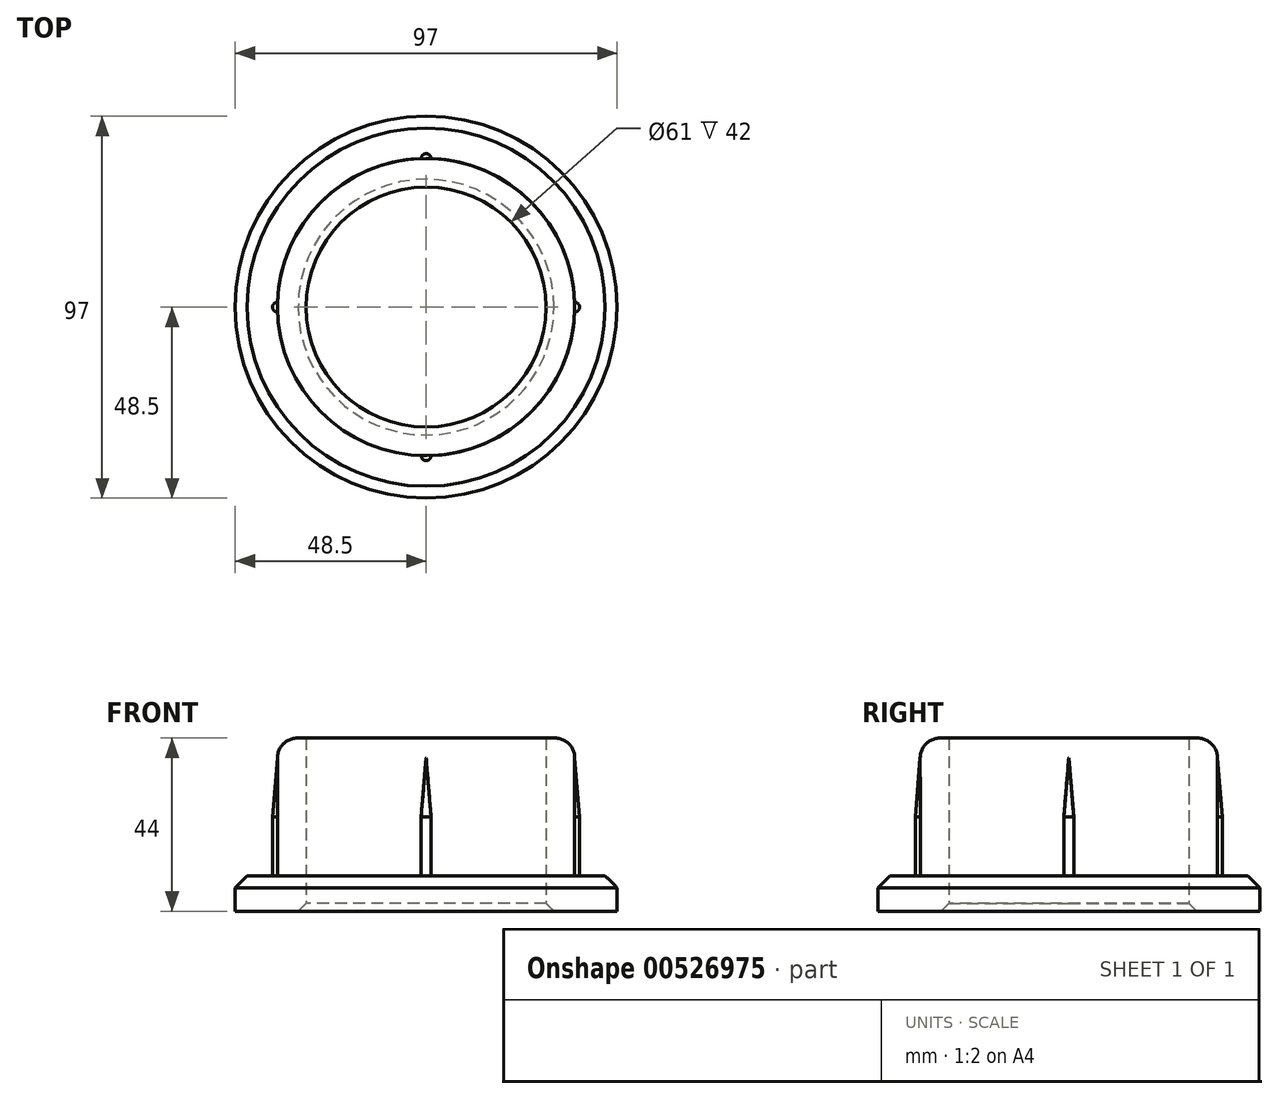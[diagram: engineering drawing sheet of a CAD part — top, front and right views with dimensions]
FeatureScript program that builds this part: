
annotation { "Feature Type Name" : "Feature", "Feature Type Description" : "" }
export const myFeature = defineFeature(function(context is Context, id is Id, definition is map)
    precondition{}
    {
        {
            var Q0;
            Q0=qCreatedBy(makeId("Top.planeOp"),FACE);
            var sketch = newSketch(context, id + "F0", { "sketchPlane" : qUnion([Q0])});
            skCircle(sketch, "E0", {"center": v(0, 0) * mm, "radius": 48.5 * mm});
            skCircle(sketch, "E1", {"center": v(0, 0) * mm, "radius": 30.5 * mm});
            skSolve(sketch);
        }
        {
            var Q0;
            Q0=makeQuery(id+"F0.imprint","IMPRINT",FACE,{"disambiguationData":[TD([[makeQuery(id+"F0.imprint","IMPRINT",EDGE,{"derivedFrom":sQuery(id+"F0.wireOp",EDGE,"E0")}),1.0]])]});
            extrude(context, id + "F1", {"entities" : qUnion([Q0]), "depth" : 9 * mm, "offsetDistance" : 25 * mm});
        }
        {
            var Q0;
            Q0=makeQuery(id+"F1.opExtrude","CAP_FACE",FACE,{"disambiguationData":[OSD([sQuery(id+"F0.wireOp",EDGE,"E0"),sQuery(id+"F0.wireOp",EDGE,"E1")])],"isStart":false});
            var sketch = newSketch(context, id + "F2", { "sketchPlane" : qUnion([Q0])});
            skCircle(sketch, "E2", {"center": v(0, 0) * mm, "radius": 30.5 * mm});
            skCircle(sketch, "E3", {"center": v(0, 0) * mm, "radius": 37.75 * mm});
            skSolve(sketch);
        }
        {
            var Q0;
            Q0=makeQuery(id+"F2.imprint","IMPRINT",FACE,{"disambiguationData":[TD([[makeQuery(id+"F2.imprint","IMPRINT",EDGE,{"derivedFrom":sQuery(id+"F2.wireOp",EDGE,"E2")}),-1.0]])]});
            extrude(context, id + "F3", {"entities" : qUnion([Q0]), "operationType" : NewBodyOperationType.ADD, "depth" : 35 * mm, "offsetDistance" : 25 * mm});
        }
        {
            var Q0;
            Q0=makeQuery(id+"F3.opExtrude","CAP_EDGE",EDGE,{"disambiguationData":[OSD([sQuery(id+"F2.wireOp",EDGE,"E3")])],"isStart":false});
            fillet(context, id + "F4", {"entities" : qUnion([Q0]), "radius" : 5 * mm, "tangentPropagation" : true, "allowEdgeOverflow" : false});
        }
        {
            var Q0;
            Q0=makeQuery(id+"F1.opExtrude","CAP_FACE",FACE,{"disambiguationData":[OSD([sQuery(id+"F0.wireOp",EDGE,"E0"),sQuery(id+"F0.wireOp",EDGE,"E1")])],"isStart":false});
            var sketch = newSketch(context, id + "F5", { "sketchPlane" : qUnion([Q0])});
            skCircle(sketch, "E4", {"center": v(0, 37.75) * mm, "radius": 1.25 * mm});
            skCircle(sketch, "E5", {"center": v(-37.75, 0) * mm, "radius": 1.25 * mm});
            skCircle(sketch, "E6", {"center": v(0, -37.75) * mm, "radius": 1.25 * mm});
            skCircle(sketch, "E7", {"center": v(37.75, 0) * mm, "radius": 1.25 * mm});
            skSolve(sketch);
        }
        {
            var Q0;
            Q0 = qSketchRegion(id + "F5", true);
            extrude(context, id + "F6", {"entities" : qUnion([Q0]), "operationType" : NewBodyOperationType.ADD, "depth" : 30 * mm, "offsetDistance" : 25 * mm});
        }
        {
            var Q0;
            Q0=makeQuery(id+"F6.opExtrude","CAP_EDGE",EDGE,{"disambiguationData":[OSD([sQuery(id+"F5.wireOp",EDGE,"E5")])],"isStart":false});
            var Q1;
            Q1=makeQuery(id+"F6.opExtrude","CAP_EDGE",EDGE,{"disambiguationData":[OSD([sQuery(id+"F5.wireOp",EDGE,"E4")])],"isStart":false});
            var Q2;
            Q2=makeQuery(id+"F6.opExtrude","CAP_EDGE",EDGE,{"disambiguationData":[OSD([sQuery(id+"F5.wireOp",EDGE,"E6")])],"isStart":false});
            var Q3;
            Q3=makeQuery(id+"F6.opExtrude","CAP_EDGE",EDGE,{"disambiguationData":[OSD([sQuery(id+"F5.wireOp",EDGE,"E7")])],"isStart":false});
            chamfer(context, id + "F7", {"entities" : qUnion([Q0, Q1, Q2, Q3]), "chamferType" : ChamferType.TWO_OFFSETS, "width1" : 1.25 * mm, "oppositeDirection" : false, "width2" : 15 * mm, "tangentPropagation" : true});
        }
        {
            var Q0;
            Q0=makeQuery(id+"F1.opExtrude","CAP_EDGE",EDGE,{"disambiguationData":[OSD([sQuery(id+"F0.wireOp",EDGE,"E1")])],"isStart":true});
            chamfer(context, id + "F8", {"entities" : qUnion([Q0]), "width" : 2 * mm, "tangentPropagation" : true});
        }
        {
            var Q0;
            Q0=makeQuery(id+"F1.opExtrude","CAP_EDGE",EDGE,{"disambiguationData":[OSD([sQuery(id+"F0.wireOp",EDGE,"E0")])],"isStart":false});
            chamfer(context, id + "F9", {"entities" : qUnion([Q0]), "width" : 3 * mm, "tangentPropagation" : true});
        }
    });
